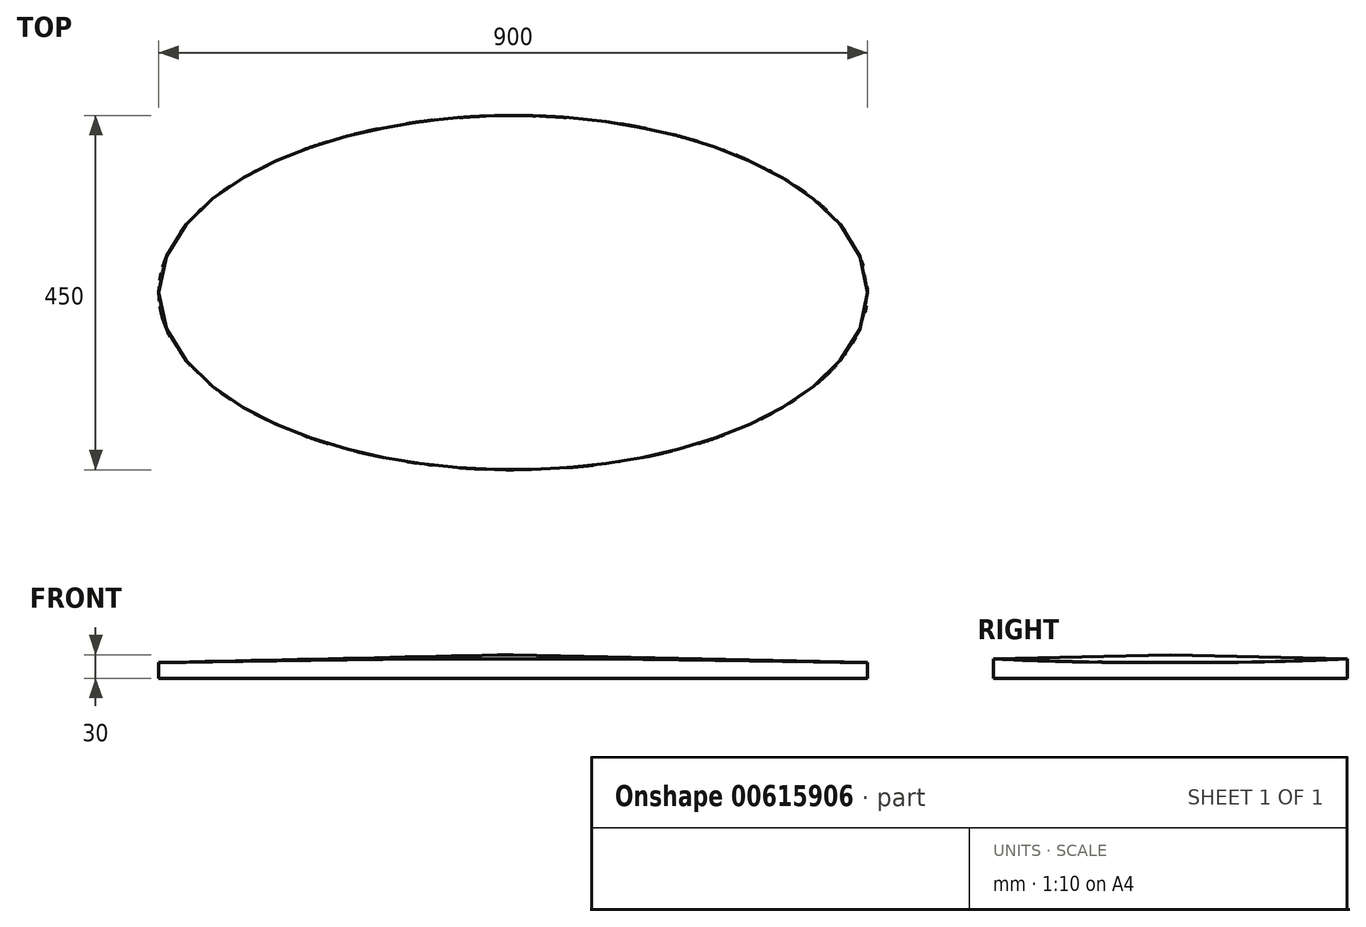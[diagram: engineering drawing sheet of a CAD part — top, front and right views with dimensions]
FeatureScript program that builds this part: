
annotation { "Feature Type Name" : "Feature", "Feature Type Description" : "" }
export const myFeature = defineFeature(function(context is Context, id is Id, definition is map)
    precondition{}
    {
        {
            var Q0;
            Q0=qCreatedBy(makeId("Front.planeOp"),FACE);
            var sketch = newSketch(context, id + "F0", { "sketchPlane" : qUnion([Q0])});
            skLineSegment(sketch, "E0.MirrorCS", {"start": v(0, 0) * mm, "end": v(-450, 0) * mm});
            skLineSegment(sketch, "E1.MirrorCS", {"start": v(-450, 0) * mm, "end": v(-450, 20) * mm});
            skLineSegment(sketch, "E2.MirrorCS", {"start": v(0, 30) * mm, "end": v(-450, 20) * mm});
            skLineSegment(sketch, "E3", {"start": v(0, 30) * mm, "end": v(0, 0) * mm});
            skSolve(sketch);
        }
        {
            var Q0;
            Q0=qSketchRegion(id+"F0",true);
            var Q1;
            Q1=sQuery(id+"F0.wireOp",EDGE,"E3");
            revolve(context, id + "F1", {"entities" : qUnion([Q0]), "axis" : qUnion([Q1]), "revolveType" : RevolveType.FULL});
        }
        {
            var Q0;
            Q0=qCreatedBy(makeId("Top.planeOp"),FACE);
            cPlane(context, id + "F2", {"entities" : qUnion([Q0]), "cplaneType" : CPlaneType.OFFSET, "offset" : 30 * mm, "width" : 150 * mm, "height" : 150 * mm});
        }
        {
            var Q0;
            Q0=qCreatedBy(id+"F2.planeOp",FACE);
            var sketch = newSketch(context, id + "F3", { "sketchPlane" : qUnion([Q0])});
            skEllipse(sketch, "E4", {"center": v(0, 0) * mm, "majorRadius": 450 * mm, "minorRadius": 225 * mm, "majorAxis": v(-1, 0)});
            skFitSpline(sketch, "E5.0", {"points": [v(-349.99, 0.63) * mm, v(-350, 0) * mm, v(-349.99, -0.63) * mm, v(-349.93, -1.5) * mm, v(-349.75, -2.7) * mm, v(-349.3, -4.53) * mm, v(-348.5, -6.88) * mm, v(-347.2, -9.82) * mm, v(-345.23, -13.39) * mm, v(-342.5, -17.54) * mm, v(-338.9, -22.23) * mm, v(-334.34, -27.39) * mm, v(-328.8, -32.92) * mm, v(-322.2, -38.75) * mm, v(-314.58, -44.8) * mm, v(-305.9, -50.99) * mm, v(-297.8, -56.2) * mm, v(-290.8, -60.36) * mm, v(-285.29, -63.48) * mm, v(-279.53, -66.58) * mm, v(-273.52, -69.66) * mm, v(-267.27, -72.7) * mm, v(-260.82, -75.7) * mm, v(-254.17, -78.64) * mm, v(-245.03, -82.48) * mm, v(-233.13, -87.11) * mm, v(-218.14, -92.38) * mm, v(-202.49, -97.33) * mm, v(-180.79, -103.47) * mm, v(-152.24, -110.22) * mm, v(-122.12, -115.62) * mm, v(-97.27, -119.07) * mm, v(-78.3, -121.2) * mm, v(-59.05, -122.89) * mm, v(-42.8, -123.9) * mm, v(-29.7, -124.47) * mm, v(-19.84, -124.77) * mm, v(-11.59, -124.93) * mm, v(-4.97, -124.99) * mm, v(0, -125) * mm, v(4.97, -124.99) * mm, v(11.59, -124.93) * mm, v(19.84, -124.77) * mm, v(29.7, -124.47) * mm, v(42.8, -123.9) * mm, v(59.05, -122.89) * mm, v(78.3, -121.2) * mm, v(97.27, -119.07) * mm, v(122.12, -115.62) * mm, v(152.24, -110.22) * mm, v(180.79, -103.47) * mm, v(202.49, -97.33) * mm, v(218.14, -92.38) * mm, v(233.13, -87.11) * mm, v(245.03, -82.48) * mm, v(254.17, -78.64) * mm, v(260.82, -75.7) * mm, v(267.27, -72.7) * mm, v(273.52, -69.66) * mm, v(279.53, -66.58) * mm, v(285.29, -63.48) * mm, v(290.8, -60.36) * mm, v(297.8, -56.2) * mm, v(305.9, -50.99) * mm, v(314.58, -44.8) * mm, v(322.2, -38.75) * mm, v(328.8, -32.92) * mm, v(334.34, -27.39) * mm, v(338.9, -22.23) * mm, v(342.5, -17.54) * mm, v(345.23, -13.39) * mm, v(347.2, -9.82) * mm, v(348.5, -6.88) * mm, v(349.3, -4.53) * mm, v(349.75, -2.7) * mm, v(349.93, -1.5) * mm, v(349.99, -0.63) * mm, v(350, 0) * mm, v(349.99, 0.63) * mm, v(349.93, 1.5) * mm, v(349.75, 2.7) * mm, v(349.3, 4.53) * mm, v(348.5, 6.88) * mm, v(347.2, 9.82) * mm, v(345.23, 13.39) * mm, v(342.5, 17.54) * mm, v(338.9, 22.23) * mm, v(334.34, 27.39) * mm, v(328.8, 32.92) * mm, v(322.2, 38.75) * mm, v(314.58, 44.8) * mm, v(305.9, 50.99) * mm, v(297.8, 56.2) * mm, v(290.8, 60.36) * mm, v(285.29, 63.48) * mm, v(279.53, 66.58) * mm, v(273.52, 69.66) * mm, v(267.27, 72.7) * mm, v(260.82, 75.7) * mm, v(254.17, 78.64) * mm, v(245.03, 82.48) * mm, v(233.13, 87.11) * mm, v(218.14, 92.38) * mm, v(202.49, 97.33) * mm, v(180.79, 103.47) * mm, v(152.24, 110.22) * mm, v(122.12, 115.62) * mm, v(97.27, 119.07) * mm, v(78.3, 121.2) * mm, v(59.05, 122.89) * mm, v(42.8, 123.9) * mm, v(29.7, 124.47) * mm, v(19.84, 124.77) * mm, v(11.59, 124.93) * mm, v(4.97, 124.99) * mm, v(0, 125) * mm, v(-4.97, 124.99) * mm, v(-11.59, 124.93) * mm, v(-19.84, 124.77) * mm, v(-29.7, 124.47) * mm, v(-42.8, 123.9) * mm, v(-59.05, 122.89) * mm, v(-78.3, 121.2) * mm, v(-97.27, 119.07) * mm, v(-122.12, 115.62) * mm, v(-152.24, 110.22) * mm, v(-180.79, 103.47) * mm, v(-202.49, 97.33) * mm, v(-218.14, 92.38) * mm, v(-233.13, 87.11) * mm, v(-245.03, 82.48) * mm, v(-254.17, 78.64) * mm, v(-260.82, 75.7) * mm, v(-267.27, 72.7) * mm, v(-273.52, 69.66) * mm, v(-279.53, 66.58) * mm, v(-285.29, 63.48) * mm, v(-290.8, 60.36) * mm, v(-297.8, 56.2) * mm, v(-305.9, 50.99) * mm, v(-314.58, 44.8) * mm, v(-322.2, 38.75) * mm, v(-328.8, 32.92) * mm, v(-334.34, 27.39) * mm, v(-338.9, 22.23) * mm, v(-342.5, 17.54) * mm, v(-345.23, 13.39) * mm, v(-347.2, 9.82) * mm, v(-348.5, 6.88) * mm, v(-349.3, 4.53) * mm, v(-349.75, 2.7) * mm, v(-349.93, 1.5) * mm, v(-349.99, 0.63) * mm, v(-350, 0) * mm, v(-349.99, -0.63) * mm, v(-349.99, 0.63) * mm]});
            skSolve(sketch);
        }
        {
            var Q0;
            Q0=qSketchRegion(id+"F3",true);
            extrude(context, id + "F4", {"entities" : qUnion([Q0]), "operationType" : NewBodyOperationType.INTERSECT, "oppositeDirection" : true, "depth" : 40 * mm, "offsetDistance" : 25 * mm});
        }
    });
